# Revit family: Plumbing-Pressure-Assist-Water-Closet-Sloan-Valve-WETS-80298016_
name_source: partatom
category: Plumbing Fixtures
units: mm (PartAtom-declared; Revit-internal decimal feet)

## family parameters
Cut with Voids When Loaded = No
Host = Face
OmniClass Number = 23.45.05.21.11.11
OmniClass Title = Water Operated Water Closets
Part Type = Normal
Room Calculation Point = No
Round Connector Dimension = Use Diameter
Shared = No

## types (3) — shared parameters
Assembly Code = D2010
CW Connection = Yes
CWFU = 10
Cold Water Connection Diameter = 1"
Cold Water Connector Description = Cold Water Connector d1/2"
Default Elevation = 0"
Depth = 30 3/8"
Edition number = 1
Flush Rate = 1.0 gpf (3.8 Lpf)
HW Connection = Yes
Height = 29 5/8"
Keynote = 15410
Manufacturer = Sloan Valve
Maximum Static Pressure = 80 PSI (552 kPa)
Minimum Static Pressure = 25 PSI (172 kPa)
Product data url = https://bimobject.com
Sanitary Drain Connection Diameter = 2"
Sanitary Drain Connector Description = Sanitary Drain Connector d2 1/8"
Tank Code = 2108016
URL = www.sloanvalve.com
Valve Pressure Drop = 0.00 psi
Vent Connection = Yes
WFU = 10
Waste Connection = Yes
Width = 18 1/4"
zero-valued in all types: HWFU

## per-type parameters (varying)
| type | Description | Part Number | Product Material | Water Closet Code |
| WETS-8029.8016 | Floor-Mounted 1.0 gpf (3.8 Lpf) ADA 12" Rough-in Pressure-Assisted/Tank Toilet. | WETS-8029.8016 | Sloan Valve - Vitreous China - White | 2108029 |
| WETS-8029.8016-BAA | Floor-Mounted 1.0 gpf (3.8 Lpf) ADA 12" Rough-in Pressure-Assisted/Tank Toilet. | 80298016 | Sloan Valve - Vitreous China - White | 2108029 |
| WETS-8029.8016-STG | Floor-Mounted 1.0 gpf (3.8 Lpf) ADA 12" Rough-in Pressure-Assisted/Tank Toilet with SloanTec® Glaze. | WETS-8029.8016-STG | Sloan Valve - Vitreous China - SloanTec Glaze White | 2178029 |

note: column(s) folded — value = type name in every type: Model

## geometry (parser evidence)
native form markers: Sweep x2
no freeform markers — native parametric forms only
